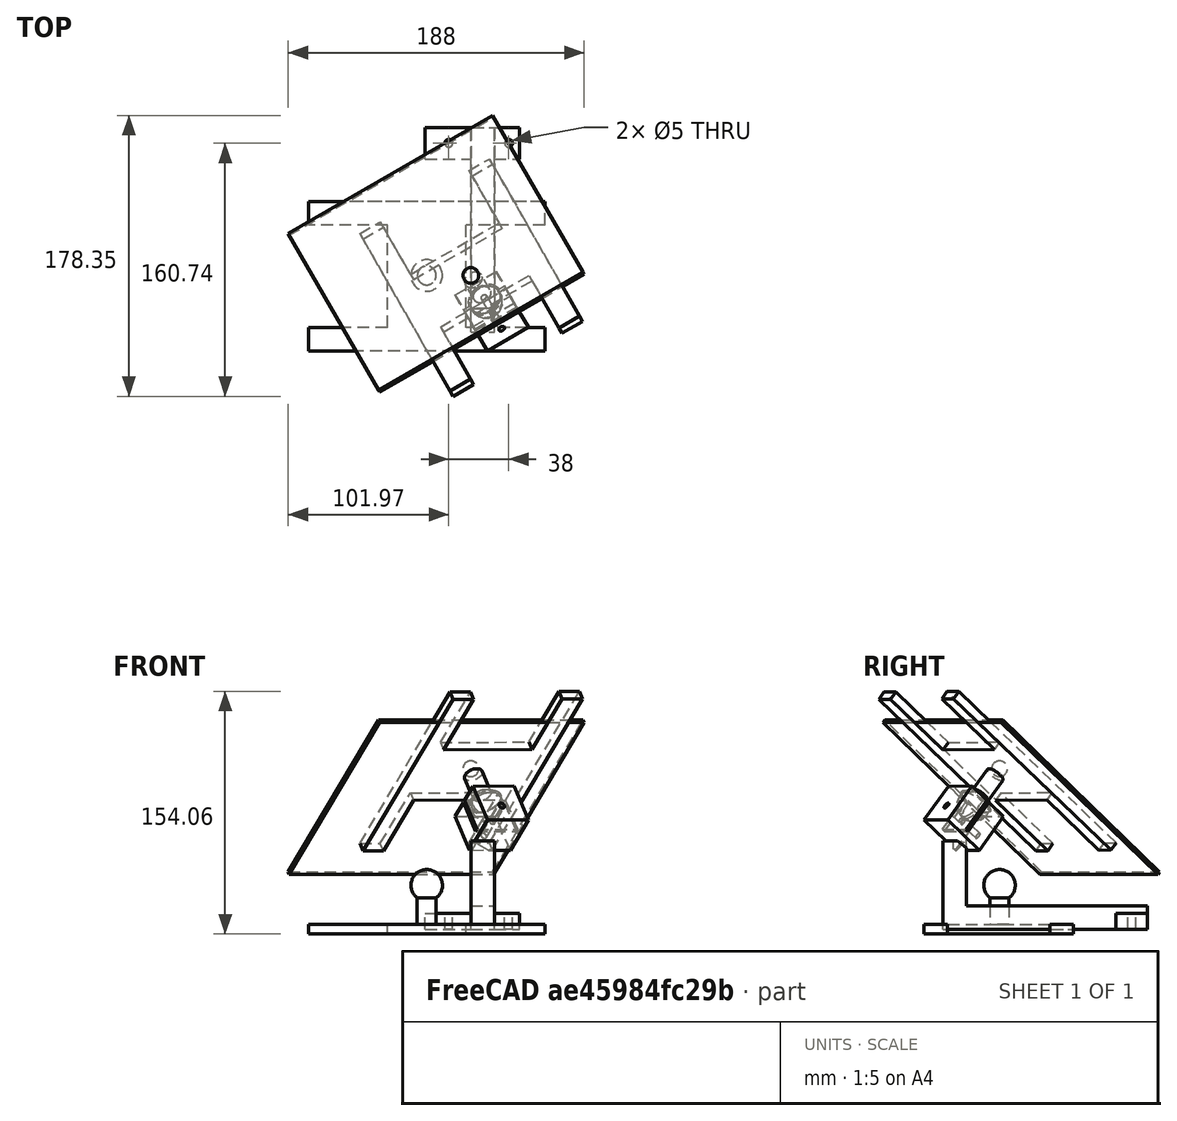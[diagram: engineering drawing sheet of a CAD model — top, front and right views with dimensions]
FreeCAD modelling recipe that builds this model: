
FCSTD DOCUMENT  (FreeCAD 0.19R24291 (Git))
Label: mirror-mount-V2
License: All rights reserved
LicenseURL: http://en.wikipedia.org/wiki/All_rights_reserved
objects: Part::Box×12, Part::MultiFuse×7, Part::Cylinder×5, Part::Cut×5, Part::Sphere×4, Part::Chamfer×1
note: 34 computed .brp shape members not serialized (recipe doc carries the construction recipe); baked Part::Feature solids carry a one-line shape summary decoded from their .brp

FEATURE [Part::Cylinder] Cylinder
  Angle = 360
  AttacherType = Attacher::AttachEngine3D
  Height = 16
  Placement = pos=(0,0,-1) rot=(0,0,1;0rad)
  Radius = 2.5
FEATURE [Part::Cylinder] Cylinder001
  Angle = 360
  AttacherType = Attacher::AttachEngine3D
  Height = 15
  Placement = pos=(38,0,-1) rot=(0,0,1;0rad)
  Radius = 2.5
FEATURE [Part::Box] Box  label="Cube"
  AttacherType = Attacher::AttachEngine3D
  Height = 10
  Length = 60
  Placement = pos=(-15,-10,0) rot=(0,0,1;0rad)
  Width = 20
FEATURE [Part::Box] Box001  label="Cube001"
  AttacherType = Attacher::AttachEngine3D
  Height = 2
  Length = 150
  Placement = pos=(-101.325,-58.5,35) rot=(-0.294262,-0.509677,-0.808479;1.24028rad)
  Width = 150
FEATURE [Part::Sphere] Sphere
  Angle1 = -90
  Angle2 = 90
  Angle3 = 360
  AttacherType = Attacher::AttachEngine3D
  Placement = pos=(14,-84,102) rot=(0,0,1;5.23599rad)
  Radius = 5
FEATURE [Part::Cylinder] Cylinder002
  Angle = 360
  AttacherType = Attacher::AttachEngine3D
  Height = 30
  Placement = pos=(14,-84,72) rot=(0,0,1;0rad)
  Radius = 6
FEATURE [Part::Sphere] Sphere001
  Angle1 = -90
  Angle2 = 90
  Angle3 = 360
  AttacherType = Attacher::AttachEngine3D
  Placement = pos=(14,-84,72) rot=(0,0,-1;1.0472rad)
  Radius = 10
FEATURE [Part::Box] Box003  label="Cube003"
  AttacherType = Attacher::AttachEngine3D
  Height = 6
  Length = 150
  Placement = pos=(-61,-52,0) rot=(0,0,1;0rad)
  Width = 15
FEATURE [Part::Box] Box004  label="Cube004"
  AttacherType = Attacher::AttachEngine3D
  Height = 6
  Length = 150
  Placement = pos=(-61,-132,0) rot=(0,0,1;0rad)
  Width = 15
FEATURE [Part::Box] Box005  label="Cube005"
  AttacherType = Attacher::AttachEngine3D
  Height = 6
  Length = 50
  Placement = pos=(-11,-125,0) rot=(0,0,1;0rad)
  Width = 81
FEATURE [Part::MultiFuse] Fusion  label="mirror-mount-1"
  Placement = pos=(0,0,97) rot=(0,0,1;0rad)
  Shapes = -> [Box003,Box004,Box005]
FEATURE [Part::Box] Box006  label="Cube006"
  AttacherType = Attacher::AttachEngine3D
  Height = 28
  Length = 30
  Placement = pos=(-1,-99,47) rot=(0,0,1;0rad)
  Width = 30
FEATURE [Part::Sphere] Sphere002
  Angle1 = -90
  Angle2 = 90
  Angle3 = 360
  AttacherType = Attacher::AttachEngine3D
  Placement = pos=(14,-84,72) rot=(0,0,-1;1.0472rad)
  Radius = 10.5
FEATURE [Part::Cut] Cut  label="ball-socket-1"
  Base = -> Box006
  Tool = -> Sphere002
FEATURE [Part::Chamfer] Chamfer  label="ball-socket-2"
  Base = -> Cut
  Edges = 1 edges r=1: [Edge10]
FEATURE [Part::Box] Box007  label="Cube007"
  AttacherType = Attacher::AttachEngine3D
  Height = 28
  Length = 2
  Placement = pos=(13,-99,51) rot=(0,0,1;0rad)
  Width = 30
FEATURE [Part::Cut] Cut001  label="ball-socket-3"
  Base = -> Chamfer
  Tool = -> Box007
FEATURE [Part::Cylinder] Cylinder003
  Angle = 360
  AttacherType = Attacher::AttachEngine3D
  Height = 40
  Placement = pos=(-7,-84,59) rot=(0,1,0;1.5708rad)
  Radius = 2
FEATURE [Part::Cut] Cut002  label="ball-socket-4"
  Base = -> Cut001
  Placement = pos=(114.414,-89.0822,15.1257) rot=(-0.289957,-0.509924,-0.809879;1.24023rad)
  Tool = -> Cylinder003
FEATURE [Part::MultiFuse] Fusion001  label="mirror-mount"
  Placement = pos=(114.414,-89.0822,15.1257) rot=(-0.289957,-0.509924,-0.809879;1.24023rad)
  Shapes = -> [Fusion,Cylinder002,Sphere001]
FEATURE [Part::Box] Box008  label="Cube008"
  AttacherType = Attacher::AttachEngine3D
  Height = 56
  Length = 15
  Placement = pos=(14,-120,0) rot=(1,0,0;0rad)
  Width = 130
FEATURE [Part::Box] Box009  label="Cube009"
  AttacherType = Attacher::AttachEngine3D
  Height = 56
  Length = 17
  Placement = pos=(13,-105,15) rot=(1,0,0;0rad)
  Width = 130
FEATURE [Part::Cut] Cut003  label="bracket-1"
  Base = -> Box008
  Tool = -> Box009
FEATURE [Part::MultiFuse] Fusion002  label="braxcket-2"
  Shapes = -> [Box,Cut003]
FEATURE [Part::MultiFuse] Fusion003  label="screw-holes"
  Shapes = -> [Cylinder,Cylinder001]
FEATURE [Part::Cut] Cut004  label="bracket-3"
  Base = -> Fusion002
  Tool = -> Fusion003
FEATURE [Part::MultiFuse] Fusion004  label="bracket"
  Shapes = -> [Cut002,Cut004]
FEATURE [Part::Box] Box010  label="Cube010"
  AttacherType = Attacher::AttachEngine3D
  Height = 6
  Length = 150
  Placement = pos=(-61,-52,0) rot=(0,0,1;0rad)
  Width = 15
FEATURE [Part::Sphere] Sphere003
  Angle1 = -90
  Angle2 = 90
  Angle3 = 360
  AttacherType = Attacher::AttachEngine3D
  Placement = pos=(14,-84,72) rot=(0,0,-1;1.0472rad)
  Radius = 10
FEATURE [Part::Cylinder] Cylinder004
  Angle = 360
  AttacherType = Attacher::AttachEngine3D
  Height = 30
  Placement = pos=(14,-84,72) rot=(0,0,1;0rad)
  Radius = 6
FEATURE [Part::Box] Box011  label="Cube011"
  AttacherType = Attacher::AttachEngine3D
  Height = 6
  Length = 150
  Placement = pos=(-61,-132,0) rot=(0,0,1;0rad)
  Width = 15
FEATURE [Part::Box] Box012  label="Cube012"
  AttacherType = Attacher::AttachEngine3D
  Height = 6
  Length = 50
  Placement = pos=(-11,-125,0) rot=(0,0,1;0rad)
  Width = 81
FEATURE [Part::MultiFuse] Fusion005  label="mirror-mount-002"
  Placement = pos=(0,0,97) rot=(0,0,1;0rad)
  Shapes = -> [Box010,Box011,Box012]
FEATURE [Part::MultiFuse] Fusion006  label="mirror-mount-for-print"
  Placement = pos=(0,0,100) rot=(0,1,0;3.14159rad)
  Shapes = -> [Fusion005,Cylinder004,Sphere003]
